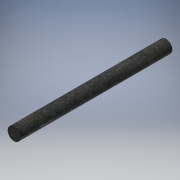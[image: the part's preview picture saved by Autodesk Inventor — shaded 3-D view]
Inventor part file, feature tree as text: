
AUTODESK INVENTOR PART (.ipt)
format: ipt  version: 2016 (Build 200138000, 138)  size: 94,208 bytes
history: native  units: in
note: dims shown in document units (in); Inventor stores cm internally (conversion verified against a paired STEP export)
features: extrude x1, sketch x1
ambient origin geometry x8: Origin, YZ Plane, XZ Plane, XY Plane, X Axis, Y Axis, Z Axis, Center Point
bodies: Solid1 (feature_tree)
feature tree (2):
  extrude  "Extrusion1"  Depth=3.0in TaperAngle=0.0deg
  sketch  "Sketch1"  dims[d0=0.25in d1=3.0in d2=0.0in]
